# Revit family: DOWNLIGHT SLIM_LSD15CW
name_source: partatom
category: Luminarias
units: mm (PartAtom-declared; Revit-internal decimal feet)

## family parameters
Compartido = No
Corte con vacíos al cargar = No
Cota de conector redondo = Diámetro de uso
Origen de luz = Sí
Punto de cálculo de habitación = No
Se basa en plano de trabajo = Sí
Siempre vertical = Sí
Tipo de pieza = Normal

## types (1)
- DOWNLIGHT SLIM_LSD15CW
    Cambio de temperatura de color de luz atenuada = <Ninguno>
    Comentarios de vataje = 90-240V
    Descripción = LUMINARIA TIPO CIRCULAR PARA EMPOTRAR EN TECHO CON CUERPO DE ALUMINIO Y VIDRIO SATINADO, IP 33 USO PARA INTERIORES CON CUERPO DE 0.77KG, CUENTA CON 1 LED TIPO 2835SMD CON UNA POTENCIA TOTAL DE 15W, A UNA TEMPERATURA EN BLANCO FRIO 4500K CON 1260 LUMENES, EFICIENCIA DE 84LM/W, IRC 80, APERTURA A 120 GRADOS EN STOCK, 300mA EN CORRIENTE DE OPERACIÓN, CON FUENTE EXTERNA REMOTAS ALIMENTADA A 90-240V.
    Elevación por defecto = 1219 mm
    Fabricante = BRILLANT
    Filtro de color = 16777215
    Longitud de símbolo de origen de luz = 500 mm  [stored 1.64042 ft]
    Lámpara = 2835 SMD
    Modelo = LSD15CW
    Watt per fixture = 15
    Ángulo de campo de foco = 120.00°
    Ángulo de enfoque = 120.00°
    Ángulo de inclinación = 60.00°

note: [stored X ft] marks values corroborated as IEEE doubles in the binary element streams (Revit-internal decimal feet)

## geometry (parser evidence)
native form markers: Blend x2
no freeform markers — native parametric forms only
